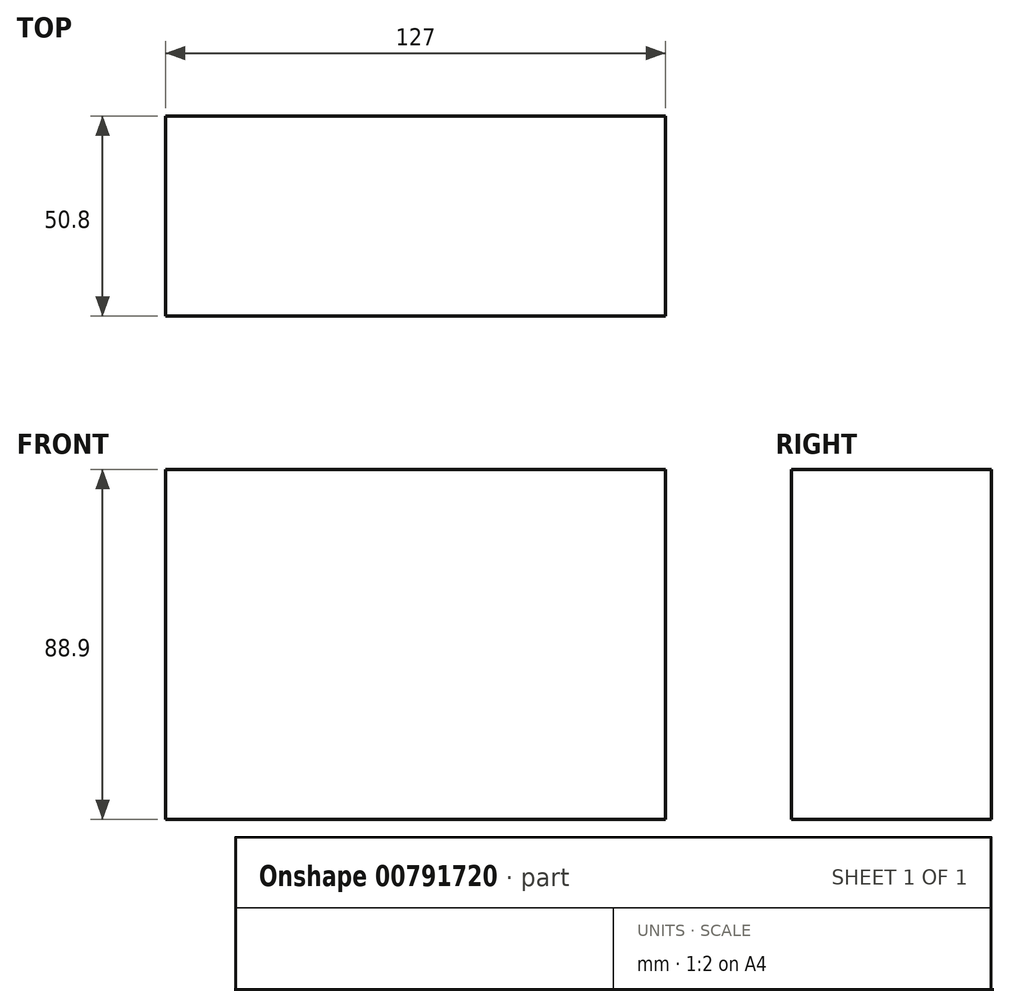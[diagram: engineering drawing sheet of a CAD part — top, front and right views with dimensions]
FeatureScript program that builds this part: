
annotation { "Feature Type Name" : "Feature", "Feature Type Description" : "" }
export const myFeature = defineFeature(function(context is Context, id is Id, definition is map)
    precondition{}
    {
        {
            var Q0;
            Q0=qCreatedBy(makeId("Front.planeOp"),FACE);
            var sketch = newSketch(context, id + "F0", { "sketchPlane" : qUnion([Q0])});
            skLineSegment(sketch, "E0.bottom", {"start": v(63.5, -44.45) * mm, "end": v(-63.5, -44.45) * mm});
            skLineSegment(sketch, "E0.top", {"start": v(63.5, 44.45) * mm, "end": v(-63.5, 44.45) * mm});
            skLineSegment(sketch, "E0.left", {"start": v(63.5, -44.45) * mm, "end": v(63.5, 44.45) * mm});
            skLineSegment(sketch, "E0.right", {"start": v(-63.5, -44.45) * mm, "end": v(-63.5, 44.45) * mm});
            skPoint(sketch, "E0.middle", {"position": v(0, 0) * mm});
            skSolve(sketch);
        }
        {
            var Q0;
            Q0=makeQuery(id+"F0.imprint","IMPRINT",FACE,{"disambiguationData":[TD([[makeQuery(id+"F0.imprint","IMPRINT",EDGE,{"derivedFrom":sQuery(id+"F0.wireOp",EDGE,"E0.bottom")}),-1.0]])]});
            extrude(context, id + "F1", {"entities" : qUnion([Q0]), "oppositeDirection" : true, "depth" : 50.8 * mm, "offsetDistance" : 25.4 * mm});
        }
    });
